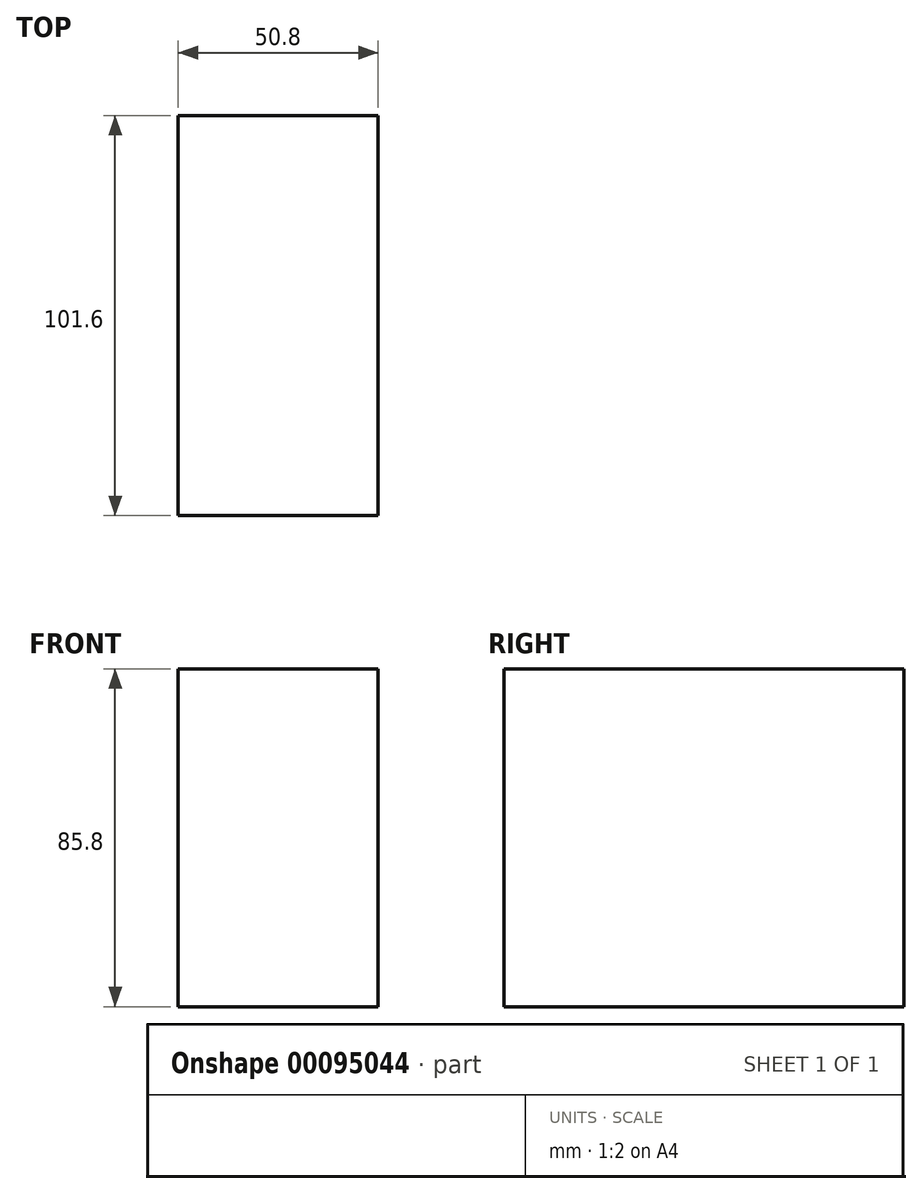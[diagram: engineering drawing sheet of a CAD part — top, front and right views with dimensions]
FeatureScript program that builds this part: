
annotation { "Feature Type Name" : "Feature", "Feature Type Description" : "" }
export const myFeature = defineFeature(function(context is Context, id is Id, definition is map)
    precondition{}
    {
        {
            var Q0;
            Q0=qCreatedBy(makeId("Front.planeOp"),FACE);
            var sketch = newSketch(context, id + "F0", { "sketchPlane" : qUnion([Q0])});
            skLineSegment(sketch, "E0.bottom", {"start": v(-44.84, 50.87) * mm, "end": v(5.96, 50.87) * mm});
            skLineSegment(sketch, "E0.top", {"start": v(-44.84, -34.93) * mm, "end": v(5.96, -34.93) * mm});
            skLineSegment(sketch, "E0.left", {"start": v(-44.84, 50.87) * mm, "end": v(-44.84, -34.93) * mm});
            skLineSegment(sketch, "E0.right", {"start": v(5.96, 50.87) * mm, "end": v(5.96, -34.93) * mm});
            skSolve(sketch);
        }
        {
            var Q0;
            Q0=makeQuery(id+"F0.imprint","IMPRINT",FACE,{"disambiguationData":[TD([[makeQuery(id+"F0.imprint","IMPRINT",EDGE,{"derivedFrom":sQuery(id+"F0.wireOp",EDGE,"E0.bottom")}),-1.0]])]});
            extrude(context, id + "F1", {"entities" : qUnion([Q0]), "endBound" : BoundingType.SYMMETRIC, "depth" : 101.6 * mm});
        }
    });
